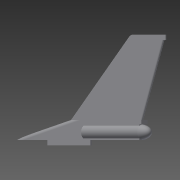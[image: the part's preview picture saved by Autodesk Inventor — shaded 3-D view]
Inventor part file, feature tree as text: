
AUTODESK INVENTOR PART (.ipt)
format: ipt  version: 2014 SP1 (Build 180222100, 222)  size: 188,928 bytes
history: native  units: mm
features: sketch x4, extrude x4, fillet x2, chamfer x1, plane x1, revolve x1
ambient origin geometry x8: Origin, YZ Plane, XZ Plane, XY Plane, X Axis, Y Axis, Z Axis, Center Point
bodies: Solid1 (feature_tree)
feature tree (13):
  sketch  "Sketch1"  dims[d0=330.0mm d1=28.0mm]
  extrude  "Extrusion1"  Depth=28.0mm
  extrude  "Extrusion2"  Depth=8.0mm
  fillet  "Fillet1"  Radius=188.0mm
  extrude  "Extrusion3"  Depth=5.0mm
  fillet  "Fillet2"  Radius=90.0mm
  extrude  "Extrusion4"  Depth=10.0mm
  chamfer  "Chamfer2"  Distance=110.0mm
  plane  "Work Plane1"
  revolve  "Revolution1"  [1 undecoded]
  sketch  "Sketch2"  dims[d2=5.0mm d3=8.0mm d4=188.0mm]
  sketch  "Sketch3"  dims[d7=10.0mm d8=5.0mm d9=90.0mm]
  sketch  "Sketch4"  dims[d10=88.0mm d11=10.0mm d12=110.0mm d13=16.0mm d14=0.0mm d15=5.0mm d16=0.0mm d17=2.5mm d18=50.0mm d19=0.0mm d23=145.0mm d24=7.9mm d25=20.0mm d26=150.0mm d27=0.0mm d28=0.0mm d29=5.9mm d30=2.0mm d31=45.0deg d32=0.0mm d33=90.0deg]
note: 1 required parameter value undecoded (feature->parameter linkage not recoverable at this tier; creation-order binding heuristic only, values carry confidence <= 0.55)
